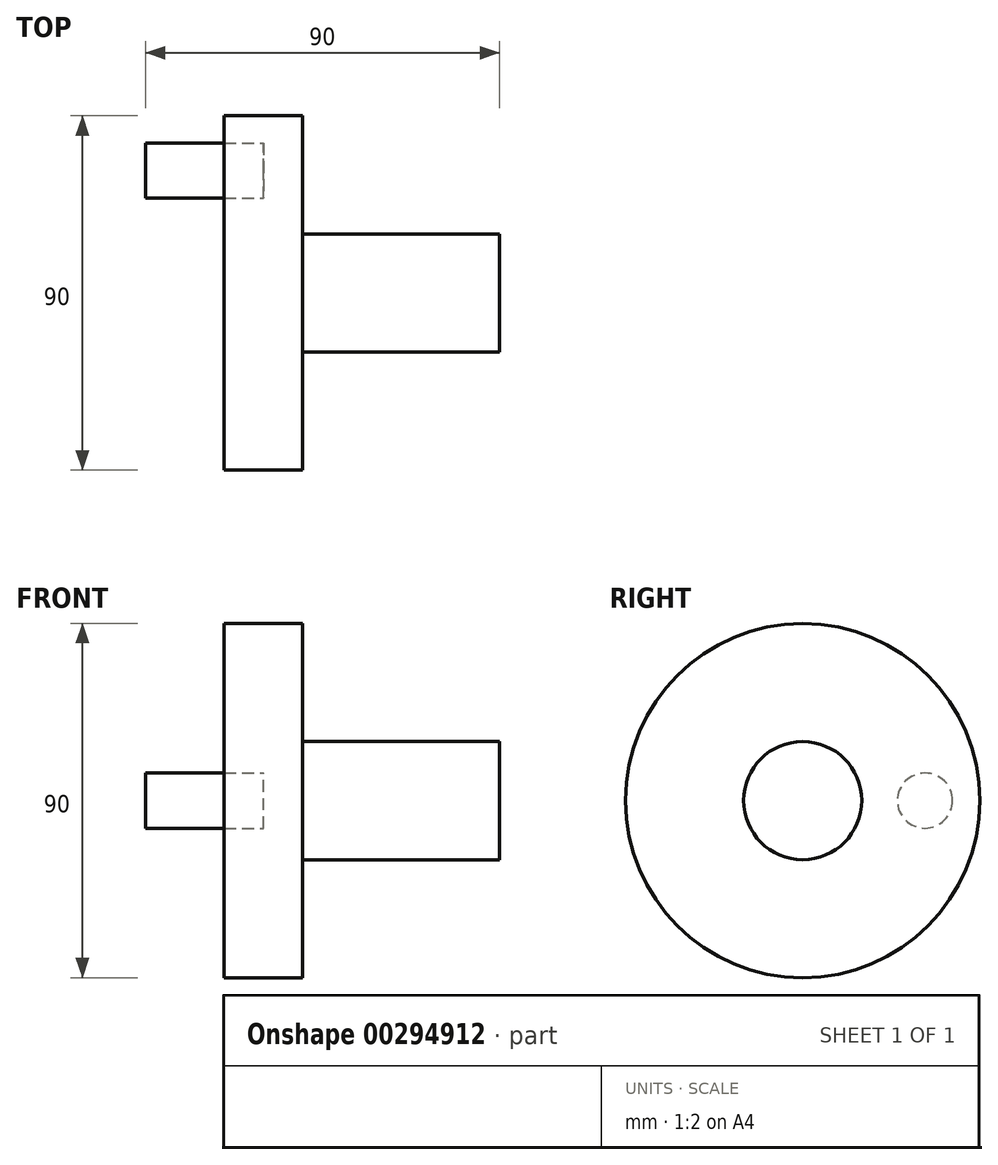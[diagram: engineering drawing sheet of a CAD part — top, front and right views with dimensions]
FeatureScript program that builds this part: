
annotation { "Feature Type Name" : "Feature", "Feature Type Description" : "" }
export const myFeature = defineFeature(function(context is Context, id is Id, definition is map)
    precondition{}
    {
        {
            var Q0;
            Q0=qCreatedBy(makeId("Right.planeOp"),FACE);
            var sketch = newSketch(context, id + "F0", { "sketchPlane" : qUnion([Q0])});
            skCircle(sketch, "E0", {"center": v(0, 0) * mm, "radius": 45 * mm});
            skLineSegment(sketch, "E1", {"start": v(0, 0) * mm, "end": v(31.06, 0) * mm});
            skCircle(sketch, "E2", {"center": v(31.06, 0) * mm, "radius": 7 * mm});
            skCircle(sketch, "E3", {"center": v(0, 0) * mm, "radius": 15 * mm});
            skSolve(sketch);
        }
        {
            var Q0;
            Q0=makeQuery(id+"F0.imprint","IMPRINT",FACE,{"disambiguationData":[TD([[makeQuery(id+"F0.imprint","IMPRINT",EDGE,{"derivedFrom":sQuery(id+"F0.wireOp",EDGE,"E0")}),1.0]])]});
            var Q1;
            Q1=makeQuery(id+"F0.imprint","IMPRINT",FACE,{"disambiguationData":[TD([[makeQuery(id+"F0.imprint","IMPRINT",EDGE,{"derivedFrom":sQuery(id+"F0.wireOp",EDGE,"E3")}),1.0]])]});
            var Q2;
            Q2=makeQuery(id+"F0.imprint","IMPRINT",FACE,{"disambiguationData":[TD([[makeQuery(id+"F0.imprint","IMPRINT",EDGE,{"derivedFrom":sQuery(id+"F0.wireOp",EDGE,"E2")}),1.0]])]});
            extrude(context, id + "F1", {"entities" : qUnion([Q0, Q1, Q2]), "endBound" : BoundingType.SYMMETRIC, "depth" : 20 * mm});
        }
        {
            var Q0;
            Q0=makeQuery(id+"F0.imprint","IMPRINT",FACE,{"disambiguationData":[TD([[makeQuery(id+"F0.imprint","IMPRINT",EDGE,{"derivedFrom":sQuery(id+"F0.wireOp",EDGE,"E3")}),1.0]])]});
            extrude(context, id + "F2", {"entities" : qUnion([Q0]), "operationType" : NewBodyOperationType.ADD, "depth" : 60 * mm});
        }
        {
            var Q0;
            Q0=makeQuery(id+"F0.imprint","IMPRINT",FACE,{"disambiguationData":[TD([[makeQuery(id+"F0.imprint","IMPRINT",EDGE,{"derivedFrom":sQuery(id+"F0.wireOp",EDGE,"E2")}),1.0]])]});
            extrude(context, id + "F3", {"entities" : qUnion([Q0]), "oppositeDirection" : true, "depth" : 30 * mm});
        }
    });
